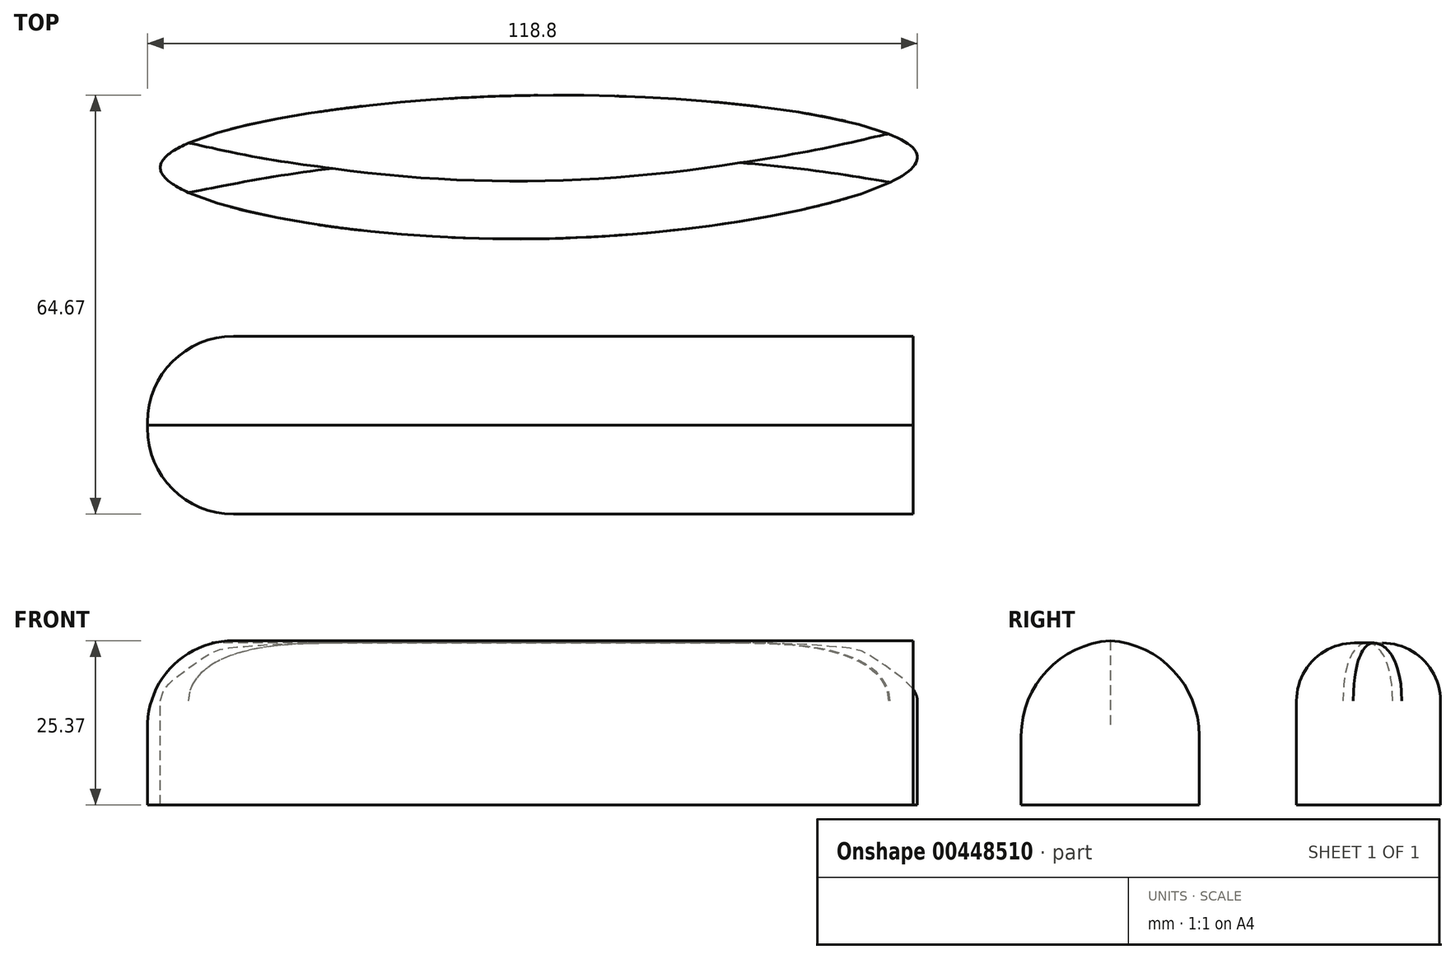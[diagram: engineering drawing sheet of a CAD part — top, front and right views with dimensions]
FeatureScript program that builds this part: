
annotation { "Feature Type Name" : "Feature", "Feature Type Description" : "" }
export const myFeature = defineFeature(function(context is Context, id is Id, definition is map)
    precondition{}
    {
        {
            var Q0;
            Q0=qCreatedBy(makeId("Top.planeOp"),FACE);
            var sketch = newSketch(context, id + "F0", { "sketchPlane" : qUnion([Q0])});
            skLineSegment(sketch, "E0.bottom", {"start": v(59.05, -13.73) * mm, "end": v(-59.05, -13.73) * mm});
            skLineSegment(sketch, "E0.top", {"start": v(59.05, 13.73) * mm, "end": v(-59.05, 13.73) * mm});
            skLineSegment(sketch, "E0.left", {"start": v(59.05, -13.73) * mm, "end": v(59.05, 13.73) * mm});
            skLineSegment(sketch, "E0.right", {"start": v(-59.05, -13.73) * mm, "end": v(-59.05, 13.73) * mm});
            skPoint(sketch, "E0.middle", {"position": v(0, 0) * mm});
            skSolve(sketch);
        }
        {
            var Q0;
            Q0=makeQuery(id+"F0.imprint","IMPRINT",FACE,{"disambiguationData":[TD([[makeQuery(id+"F0.imprint","IMPRINT",EDGE,{"derivedFrom":sQuery(id+"F0.wireOp",EDGE,"E0.bottom")}),-1.0]])]});
            extrude(context, id + "F1", {"entities" : qUnion([Q0]), "depth" : 25.4 * mm});
        }
        {
            var Q0;
            Q0=makeQuery(id+"F1.opExtrude","CAP_EDGE",EDGE,{"disambiguationData":[OSD([sQuery(id+"F0.wireOp",EDGE,"E0.bottom")])],"isStart":false});
            var Q1;
            Q1=makeQuery(id+"F1.opExtrude","CAP_EDGE",EDGE,{"disambiguationData":[OSD([sQuery(id+"F0.wireOp",EDGE,"E0.top")])],"isStart":false});
            fillet(context, id + "F2", {"entities" : qUnion([Q0, Q1]), "radius" : 14.73 * mm, "tangentPropagation" : true, "allowEdgeOverflow" : false});
        }
        {
            var Q0;
            Q0=makeQuery(id+"F2.opFillet","BLEND_EDGE",EDGE,{"blendedFrom":[makeQuery(id+"F1.opExtrude","CAP_EDGE",EDGE,{"disambiguationData":[OSD([sQuery(id+"F0.wireOp",EDGE,"E0.bottom")])],"isStart":false}),makeQuery(id+"F1.opExtrude","SWEPT_FACE",FACE,{"disambiguationData":[OSD([sQuery(id+"F0.wireOp",EDGE,"E0.right")])]})],"blendedInto":[makeQuery(id+"F1.opExtrude","SWEPT_FACE",FACE,{"disambiguationData":[OSD([sQuery(id+"F0.wireOp",EDGE,"E0.right")])]})]});
            var Q1;
            Q1=makeQuery(id+"F2.opFillet","BLEND_EDGE",EDGE,{"blendedFrom":[makeQuery(id+"F1.opExtrude","CAP_EDGE",EDGE,{"disambiguationData":[OSD([sQuery(id+"F0.wireOp",EDGE,"E0.top")])],"isStart":false}),makeQuery(id+"F1.opExtrude","SWEPT_FACE",FACE,{"disambiguationData":[OSD([sQuery(id+"F0.wireOp",EDGE,"E0.right")])]})],"blendedInto":[makeQuery(id+"F1.opExtrude","SWEPT_FACE",FACE,{"disambiguationData":[OSD([sQuery(id+"F0.wireOp",EDGE,"E0.right")])]})]});
            fillet(context, id + "F3", {"entities" : qUnion([Q0, Q1]), "radius" : 13.28 * mm, "tangentPropagation" : true, "allowEdgeOverflow" : false});
        }
        {
            var Q0;
            Q0=qCreatedBy(makeId("Top.planeOp"),FACE);
            var sketch = newSketch(context, id + "F4", { "sketchPlane" : qUnion([Q0])});
            skFitSpline(sketch, "E1", {"points": [v(-57.05, 39.77) * mm, v(0, 50.9) * mm, v(59.75, 41.36) * mm, v(0, 28.76) * mm, v(-57.05, 39.77) * mm]});
            skSolve(sketch);
        }
        {
            var Q0;
            Q0=makeQuery(id+"F4.imprint","IMPRINT",FACE,{"disambiguationData":[TD([[makeQuery(id+"F4.imprint","IMPRINT",EDGE,{"derivedFrom":sQuery(id+"F4.wireOp",EDGE,"E1")}),-1.0]])]});
            extrude(context, id + "F5", {"entities" : qUnion([Q0]), "depth" : 25 * mm});
        }
        {
            var Q0;
            Q0=makeQuery(id+"F5.opExtrude","CAP_EDGE",EDGE,{"disambiguationData":[OSD([sQuery(id+"F4.wireOp",EDGE,"E1")])],"isStart":false});
            fillet(context, id + "F6", {"entities" : qUnion([Q0]), "radius" : 8.93 * mm, "tangentPropagation" : true, "allowEdgeOverflow" : false});
        }
    });
